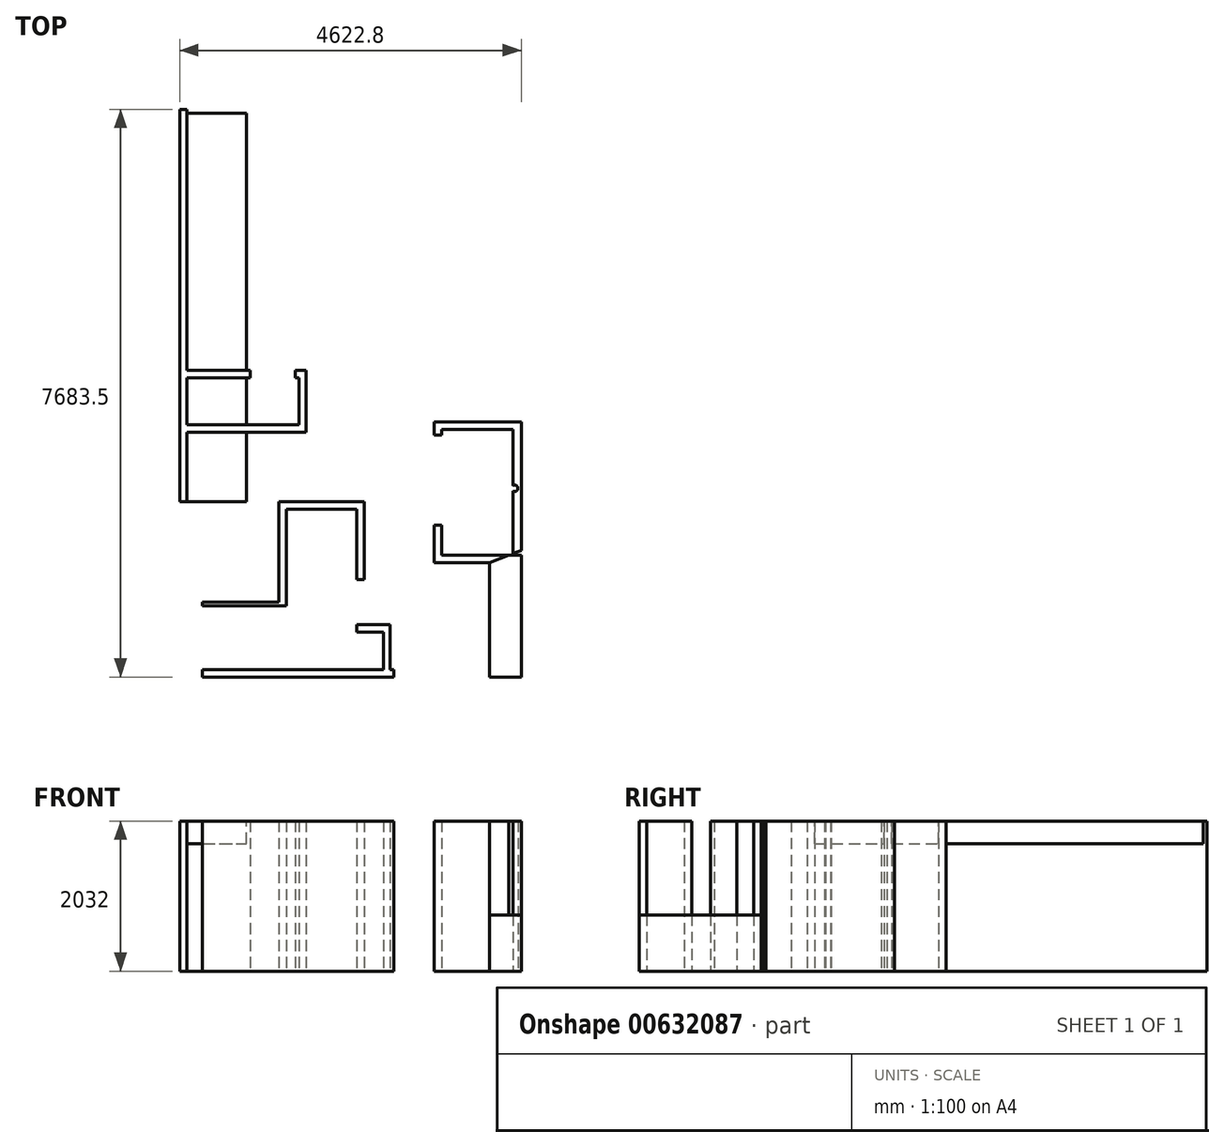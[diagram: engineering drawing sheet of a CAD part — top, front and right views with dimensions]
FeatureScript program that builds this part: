
annotation { "Feature Type Name" : "Feature", "Feature Type Description" : "" }
export const myFeature = defineFeature(function(context is Context, id is Id, definition is map)
    precondition{}
    {
        {
            var Q0;
            Q0=qCreatedBy(makeId("Top.planeOp"),FACE);
            var sketch = newSketch(context, id + "F0", { "sketchPlane" : qUnion([Q0])});
            skLineSegment(sketch, "E0.bottom", {"start": v(-1181.1, 196.84) * mm, "end": v(0, 196.84) * mm});
            skLineSegment(sketch, "E0.top", {"start": v(-1079.5, 95.24) * mm, "end": v(-114.3, 95.24) * mm});
            skLineSegment(sketch, "E0.left", {"start": v(-1181.1, 196.84) * mm, "end": v(-1181.1, 95.24) * mm});
            skLineSegment(sketch, "E0.right", {"start": v(0, 196.84) * mm, "end": v(0, 95.24) * mm});
            skLineSegment(sketch, "E1", {"start": v(0, 95.24) * mm, "end": v(0, -1695.46) * mm});
            skLineSegment(sketch, "E2.top", {"start": v(-1181.1, 19.04) * mm, "end": v(-1079.5, 19.04) * mm});
            skLineSegment(sketch, "E2.left", {"start": v(-1181.1, 95.24) * mm, "end": v(-1181.1, 19.04) * mm});
            skLineSegment(sketch, "E2.right", {"start": v(-1079.5, 95.24) * mm, "end": v(-1079.5, 19.04) * mm});
            skLineSegment(sketch, "E3", {"start": v(0, -1695.46) * mm, "end": v(0, -3257.56) * mm});
            skLineSegment(sketch, "E4", {"start": v(0, -3257.56) * mm, "end": v(-431.8, -3257.56) * mm});
            skLineSegment(sketch, "E5.bottom", {"start": v(-158.6, -632.74) * mm, "end": v(-1022.2, -632.74) * mm});
            skLineSegment(sketch, "E5.top", {"start": v(-158.6, 53.06) * mm, "end": v(-1022.2, 53.06) * mm});
            skLineSegment(sketch, "E5.left", {"start": v(-158.6, -632.74) * mm, "end": v(-158.6, 53.06) * mm});
            skLineSegment(sketch, "E5.right", {"start": v(-1022.2, -632.74) * mm, "end": v(-1022.2, 53.06) * mm});
            skLineSegment(sketch, "E6", {"start": v(-431.8, -3257.56) * mm, "end": v(-914.4, -3257.56) * mm});
            skLineSegment(sketch, "E7.bottom", {"start": v(-914.4, -3257.56) * mm, "end": v(-1727.2, -3257.56) * mm});
            skLineSegment(sketch, "E7.top", {"start": v(-914.4, -3192.68) * mm, "end": v(-1727.2, -3192.68) * mm});
            skLineSegment(sketch, "E7.left", {"start": v(-914.4, -3257.56) * mm, "end": v(-914.4, -3192.68) * mm});
            skLineSegment(sketch, "E7.right", {"start": v(-1727.2, -3257.56) * mm, "end": v(-1727.2, -3192.68) * mm});
            skLineSegment(sketch, "E8.bottom", {"start": v(-1727.2, -3257.56) * mm, "end": v(-4127.5, -3257.56) * mm});
            skLineSegment(sketch, "E8.top", {"start": v(-1727.2, -3155.96) * mm, "end": v(-1778, -3155.96) * mm});
            skLineSegment(sketch, "E8.left", {"start": v(-1727.2, -3257.56) * mm, "end": v(-1727.2, -3155.96) * mm});
            skLineSegment(sketch, "E9.top", {"start": v(-1778, -2546.36) * mm, "end": v(-1866.9, -2546.36) * mm});
            skLineSegment(sketch, "E9.left", {"start": v(-1778, -3155.96) * mm, "end": v(-1778, -2546.36) * mm});
            skLineSegment(sketch, "E9.right", {"start": v(-1866.9, -3155.96) * mm, "end": v(-1866.9, -2647.96) * mm});
            skLineSegment(sketch, "E10", {"start": v(-4127.5, -3257.56) * mm, "end": v(-4622.8, -3257.56) * mm});
            skLineSegment(sketch, "E11.bottom", {"start": v(-4127.5, -2292.36) * mm, "end": v(-3175, -2292.36) * mm});
            skLineSegment(sketch, "E11.top", {"start": v(-4127.5, -2241.56) * mm, "end": v(-3276.6, -2241.56) * mm});
            skLineSegment(sketch, "E11.right", {"start": v(-3175, -2292.36) * mm, "end": v(-3175, -2241.56) * mm});
            skLineSegment(sketch, "E12.trimOffspring", {"start": v(-1866.9, -3155.96) * mm, "end": v(-4127.5, -3155.96) * mm});
            skLineSegment(sketch, "E13", {"start": v(-4622.8, -3257.56) * mm, "end": v(-4622.8, 578.48) * mm});
            skLineSegment(sketch, "E14.bottom", {"start": v(-1866.9, -2546.36) * mm, "end": v(-2038.07, -2546.36) * mm});
            skLineSegment(sketch, "E14.top", {"start": v(-1866.9, -2647.96) * mm, "end": v(-2038.07, -2647.96) * mm});
            skArc(sketch, "E15", {"start": v(-1727.2, -3155.96) * mm, "mid": v(-1476.59, -2604.52) * mm, "end": v(-914.4, -2379.05) * mm});
            skLineSegment(sketch, "E16.bottom", {"start": v(-721.37, -1068) * mm, "end": v(-213.37, -1068) * mm});
            skLineSegment(sketch, "E16.top", {"start": v(-721.37, -1576) * mm, "end": v(-213.37, -1576) * mm});
            skLineSegment(sketch, "E16.left", {"start": v(-721.37, -1068) * mm, "end": v(-721.37, -1576) * mm});
            skLineSegment(sketch, "E16.right", {"start": v(-213.37, -1068) * mm, "end": v(-213.37, -1576) * mm});
            skLineSegment(sketch, "E17", {"start": v(-431.8, -3257.56) * mm, "end": v(-431.8, -1708.16) * mm});
            skLineSegment(sketch, "E18", {"start": v(0, -1543.06) * mm, "end": v(-431.8, -1708.16) * mm});
            skLineSegment(sketch, "E19", {"start": v(-3276.6, -2241.56) * mm, "end": v(-3276.6, -882.66) * mm});
            skLineSegment(sketch, "E20", {"start": v(-3175, -2241.56) * mm, "end": v(-3175, -984.26) * mm});
            skLineSegment(sketch, "E21", {"start": v(-2120.9, -882.66) * mm, "end": v(-3009.9, -882.66) * mm});
            skLineSegment(sketch, "E22", {"start": v(-3175, -984.26) * mm, "end": v(-2222.5, -984.26) * mm});
            skLineSegment(sketch, "E23", {"start": v(-2222.5, -984.26) * mm, "end": v(-2222.5, -984.26) * mm});
            skLineSegment(sketch, "E24", {"start": v(-2120.9, -882.66) * mm, "end": v(-2120.9, -1936.76) * mm});
            skLineSegment(sketch, "E25", {"start": v(-2222.5, -984.26) * mm, "end": v(-2222.5, -1936.76) * mm});
            skLineSegment(sketch, "E26", {"start": v(-2222.5, -1936.76) * mm, "end": v(-2120.9, -1936.76) * mm});
            skArc(sketch, "E27", {"start": v(-2730.5, -1936.76) * mm, "mid": v(-2551.95, -2367.81) * mm, "end": v(-2120.9, -2546.36) * mm});
            skLineSegment(sketch, "E28", {"start": v(-1079.5, -1606.56) * mm, "end": v(0, -1606.56) * mm});
            skCircle(sketch, "E29", {"center": v(-88.9, -704.86) * mm, "radius": 44.45 * mm});
            skLineSegment(sketch, "E30", {"start": v(-431.8, -1708.16) * mm, "end": v(-1181.1, -1708.16) * mm});
            skLineSegment(sketch, "E31", {"start": v(-1181.1, -1708.16) * mm, "end": v(-1181.1, -1403.36) * mm});
            skLineSegment(sketch, "E32", {"start": v(-1079.5, -1403.36) * mm, "end": v(-1079.5, -1606.56) * mm});
            skLineSegment(sketch, "E33", {"start": v(-114.3, 95.24) * mm, "end": v(-114.3, -631.37) * mm});
            skLineSegment(sketch, "E34", {"start": v(-1181.1, -1403.36) * mm, "end": v(-1181.1, -1200.16) * mm});
            skLineSegment(sketch, "E35", {"start": v(-1181.1, -1200.16) * mm, "end": v(-1079.5, -1200.16) * mm});
            skLineSegment(sketch, "E36", {"start": v(-1079.5, -1200.16) * mm, "end": v(-1079.5, -1403.36) * mm});
            skLineSegment(sketch, "E37", {"start": v(-114.3, -631.37) * mm, "end": v(-114.3, -1606.56) * mm});
            skPoint(sketch, "E38.end.orphan", {"position": v(0, -631.37) * mm});
            skLineSegment(sketch, "E39", {"start": v(-2038.07, -2546.36) * mm, "end": v(-2222.5, -2546.36) * mm});
            skLineSegment(sketch, "E40", {"start": v(-2222.5, -2546.36) * mm, "end": v(-2222.5, -2647.96) * mm});
            skLineSegment(sketch, "E41", {"start": v(-2222.5, -2647.96) * mm, "end": v(-2038.07, -2647.96) * mm});
            skLineSegment(sketch, "E42", {"start": v(-4127.5, -3155.96) * mm, "end": v(-4318, -3155.96) * mm});
            skLineSegment(sketch, "E43", {"start": v(-4318, -3155.96) * mm, "end": v(-4318, -3257.56) * mm});
            skLineSegment(sketch, "E44", {"start": v(-4318, -3155.96) * mm, "end": v(-4318, -2292.36) * mm});
            skLineSegment(sketch, "E45", {"start": v(-4318, -2292.36) * mm, "end": v(-4127.5, -2292.36) * mm});
            skLineSegment(sketch, "E46", {"start": v(-4127.5, -2241.56) * mm, "end": v(-4318, -2241.56) * mm});
            skLineSegment(sketch, "E47", {"start": v(-4318, -2241.56) * mm, "end": v(-4318, -2292.36) * mm});
            skArc(sketch, "E48", {"start": v(-1181.1, -590.56) * mm, "mid": v(-1612.15, -412.01) * mm, "end": v(-1790.7, 19.04) * mm});
            skArc(sketch, "E49", {"start": v(-1181.1, -590.56) * mm, "mid": v(-1612.15, -769.1) * mm, "end": v(-1790.7, -1200.16) * mm});
            skLineSegment(sketch, "E50.bottom", {"start": v(-3276.6, 57.14) * mm, "end": v(-2908.3, 57.14) * mm});
            skLineSegment(sketch, "E50.top", {"start": v(-3111.5, 158.74) * mm, "end": v(-3009.9, 158.74) * mm});
            skLineSegment(sketch, "E50.right", {"start": v(-2908.3, 57.14) * mm, "end": v(-2908.3, 158.74) * mm});
            skLineSegment(sketch, "E51.bottom", {"start": v(-4622.8, -882.66) * mm, "end": v(-4521.2, -882.66) * mm});
            skLineSegment(sketch, "E51.top", {"start": v(-4622.8, 4425.94) * mm, "end": v(-4521.2, 4425.94) * mm});
            skLineSegment(sketch, "E51.left", {"start": v(-4622.8, -882.66) * mm, "end": v(-4622.8, 4425.94) * mm});
            skLineSegment(sketch, "E51.right", {"start": v(-4521.2, -882.66) * mm, "end": v(-4521.2, 57.14) * mm});
            skLineSegment(sketch, "E52.bottom", {"start": v(-3111.5, 158.74) * mm, "end": v(-4521.2, 158.74) * mm});
            skLineSegment(sketch, "E52.top", {"start": v(-3276.6, 57.14) * mm, "end": v(-4521.2, 57.14) * mm});
            skLineSegment(sketch, "E53.trimOffspring", {"start": v(-4521.2, 158.74) * mm, "end": v(-4521.2, 793.74) * mm});
            skLineSegment(sketch, "E54", {"start": v(-3276.6, -882.66) * mm, "end": v(-3009.9, -882.66) * mm});
            skLineSegment(sketch, "E55.bottom", {"start": v(-2908.3, -882.66) * mm, "end": v(-3009.9, -882.66) * mm});
            skLineSegment(sketch, "E55.top", {"start": v(-2908.3, -819.16) * mm, "end": v(-3009.9, -819.16) * mm});
            skLineSegment(sketch, "E55.left", {"start": v(-2908.3, -882.66) * mm, "end": v(-2908.3, -819.16) * mm});
            skLineSegment(sketch, "E55.right", {"start": v(-3009.9, -882.66) * mm, "end": v(-3009.9, -819.16) * mm});
            skPoint(sketch, "E56.oppositeSnap0", {"position": v(-3009.9, 158.74) * mm});
            skLineSegment(sketch, "E56.top", {"start": v(-2908.3, 895.34) * mm, "end": v(-3009.9, 895.34) * mm});
            skLineSegment(sketch, "E56.left", {"start": v(-2908.3, 158.74) * mm, "end": v(-2908.3, 895.34) * mm});
            skLineSegment(sketch, "E56.right", {"start": v(-3009.9, 158.74) * mm, "end": v(-3009.9, 793.74) * mm});
            skLineSegment(sketch, "E57.bottom", {"start": v(-3009.9, 895.34) * mm, "end": v(-3060.7, 895.34) * mm});
            skLineSegment(sketch, "E57.top", {"start": v(-3009.9, 793.74) * mm, "end": v(-3060.7, 793.74) * mm});
            skLineSegment(sketch, "E57.right", {"start": v(-3060.7, 895.34) * mm, "end": v(-3060.7, 793.74) * mm});
            skLineSegment(sketch, "E58.bottom", {"start": v(-3670.3, 895.34) * mm, "end": v(-4521.2, 895.34) * mm});
            skLineSegment(sketch, "E58.top", {"start": v(-3670.3, 793.74) * mm, "end": v(-4521.2, 793.74) * mm});
            skLineSegment(sketch, "E58.left", {"start": v(-3670.3, 895.34) * mm, "end": v(-3670.3, 793.74) * mm});
            skLineSegment(sketch, "E59.trimOffspring", {"start": v(-4521.2, 895.34) * mm, "end": v(-4521.2, 4425.94) * mm});
            skArc(sketch, "E60", {"start": v(-2908.3, 57.14) * mm, "mid": v(-2288.66, -199.52) * mm, "end": v(-2032, -819.16) * mm});
            skArc(sketch, "E61", {"start": v(-3060.7, 895.34) * mm, "mid": v(-3239.25, 1326.4) * mm, "end": v(-3670.3, 1504.94) * mm});
            skLineSegment(sketch, "E62.bottom", {"start": v(-2908.3, 57.14) * mm, "end": v(-3009.9, 57.14) * mm});
            skLineSegment(sketch, "E62.top", {"start": v(-2908.3, -6.36) * mm, "end": v(-3009.9, -6.36) * mm});
            skLineSegment(sketch, "E62.left", {"start": v(-2908.3, 57.14) * mm, "end": v(-2908.3, -6.36) * mm});
            skLineSegment(sketch, "E62.right", {"start": v(-3009.9, 57.14) * mm, "end": v(-3009.9, -6.36) * mm});
            skSolve(sketch);
        }
        {
            var Q0;
            Q0=makeQuery(id+"F0.imprint","IMPRINT",FACE,{"disambiguationData":[TD([[makeQuery(id+"F0.imprint","IMPRINT",EDGE,{"derivedFrom":sQuery(id+"F0.wireOp",EDGE,"E0.bottom")}),-1.0]])]});
            var Q1;
            {var subQ0=sQuery(id+"F0.wireOp",EDGE,"E30");Q1=makeQuery(id+"F0.imprint","IMPRINT",FACE,{"disambiguationData":[TD([[makeQuery(id+"F0.imprint","IMPRINT",EDGE,{"derivedFrom":subQ0}),-1.0]])]});}
            var Q2;
            Q2=makeQuery(id+"F0.imprint","IMPRINT",FACE,{"disambiguationData":[TD([[makeQuery(id+"F0.imprint","IMPRINT",EDGE,{"derivedFrom":sQuery(id+"F0.wireOp",EDGE,"E11.bottom")}),1.0]])]});
            var Q3;
            {var subQ1=sQuery(id+"F0.wireOp",EDGE,"E8.bottom");Q3=makeQuery(id+"F0.imprint","IMPRINT",FACE,{"disambiguationData":[TD([[makeQuery(id+"F0.imprint","IMPRINT",EDGE,{"derivedFrom":subQ1}),-1.0]])]});}
            var Q4;
            Q4=makeQuery(id+"F0.imprint","IMPRINT",FACE,{"disambiguationData":[TD([[makeQuery(id+"F0.imprint","IMPRINT",EDGE,{"derivedFrom":sQuery(id+"F0.wireOp",EDGE,"E50.bottom")}),1.0]])]});
            var Q5;
            Q5=makeQuery(id+"F0.imprint","IMPRINT",FACE,{"disambiguationData":[TD([[makeQuery(id+"F0.imprint","IMPRINT",EDGE,{"derivedFrom":sQuery(id+"F0.wireOp",EDGE,"E55.bottom")}),-1.0]])]});
            extrude(context, id + "F1", {"entities" : qUnion([Q0, Q1, Q2, Q3, Q4, Q5]), "depth" : 2032 * mm, "offsetDistance" : 25.4 * mm});
        }
        {
            var Q0;
            Q0=makeQuery(id+"F1.opExtrude","CAP_FACE",FACE,{"disambiguationData":[OSD([sQuery(id+"F0.wireOp",EDGE,"E50.bottom"),sQuery(id+"F0.wireOp",EDGE,"E50.top"),sQuery(id+"F0.wireOp",EDGE,"E50.right"),sQuery(id+"F0.wireOp",EDGE,"E51.bottom"),sQuery(id+"F0.wireOp",EDGE,"E51.top"),sQuery(id+"F0.wireOp",EDGE,"E51.left"),sQuery(id+"F0.wireOp",EDGE,"E51.right"),sQuery(id+"F0.wireOp",EDGE,"E52.bottom"),sQuery(id+"F0.wireOp",EDGE,"E52.top"),sQuery(id+"F0.wireOp",EDGE,"E53.trimOffspring"),sQuery(id+"F0.wireOp",EDGE,"E56.top"),sQuery(id+"F0.wireOp",EDGE,"E56.left"),sQuery(id+"F0.wireOp",EDGE,"E56.right"),sQuery(id+"F0.wireOp",EDGE,"E57.bottom"),sQuery(id+"F0.wireOp",EDGE,"E57.top"),sQuery(id+"F0.wireOp",EDGE,"E57.right"),sQuery(id+"F0.wireOp",EDGE,"E58.bottom"),sQuery(id+"F0.wireOp",EDGE,"E58.top"),sQuery(id+"F0.wireOp",EDGE,"E58.left"),sQuery(id+"F0.wireOp",EDGE,"E59.trimOffspring")])],"isStart":false});
            var sketch = newSketch(context, id + "F2", { "sketchPlane" : qUnion([Q0])});
            skLineSegment(sketch, "E63.bottom", {"start": v(-4521.2, -882.66) * mm, "end": v(-3721.1, -882.66) * mm});
            skLineSegment(sketch, "E63.top", {"start": v(-4521.2, 4375.14) * mm, "end": v(-3721.1, 4375.14) * mm});
            skLineSegment(sketch, "E63.left", {"start": v(-4521.2, -882.66) * mm, "end": v(-4521.2, 4375.14) * mm});
            skLineSegment(sketch, "E63.right", {"start": v(-3721.1, -882.66) * mm, "end": v(-3721.1, 4375.14) * mm});
            skSolve(sketch);
        }
        {
            var Q0;
            {var subQ0=sQuery(id+"F2.wireOp",EDGE,"E63.top");Q0=makeQuery(id+"F2.imprint","IMPRINT",FACE,{"disambiguationData":[TD([[makeQuery(id+"F2.imprint","IMPRINT",EDGE,{"derivedFrom":subQ0}),-1.0]])]});}
            var Q1;
            {var subQ3=makeQuery(id+"F1.opExtrude","CAP_EDGE",EDGE,{"disambiguationData":[OSD([sQuery(id+"F0.wireOp",EDGE,"E58.top")])],"isStart":false});Q1=makeQuery(id+"F2.imprint","IMPRINT",FACE,{"disambiguationData":[TD([[makeQuery(id+"F2.imprint","IMPRINT",EDGE,{"derivedFrom":subQ3}),1.0]])]});}
            var Q2;
            {var subQ0=sQuery(id+"F2.wireOp",EDGE,"E63.bottom");Q2=makeQuery(id+"F2.imprint","IMPRINT",FACE,{"disambiguationData":[TD([[makeQuery(id+"F2.imprint","IMPRINT",EDGE,{"derivedFrom":subQ0}),1.0]])]});}
            extrude(context, id + "F3", {"entities" : qUnion([Q0, Q1, Q2]), "oppositeDirection" : true, "depth" : 304.8 * mm, "offsetDistance" : 25.4 * mm});
        }
        {
            var Q0;
            {var subQ1=sQuery(id+"F0.wireOp",EDGE,"E3");Q0=makeQuery(id+"F0.imprint","IMPRINT",FACE,{"disambiguationData":[TD([[makeQuery(id+"F0.imprint","IMPRINT",EDGE,{"derivedFrom":subQ1}),-1.0]])]});}
            extrude(context, id + "F4", {"entities" : qUnion([Q0]), "operationType" : NewBodyOperationType.ADD, "depth" : 762 * mm, "offsetDistance" : 25.4 * mm});
        }
    });
